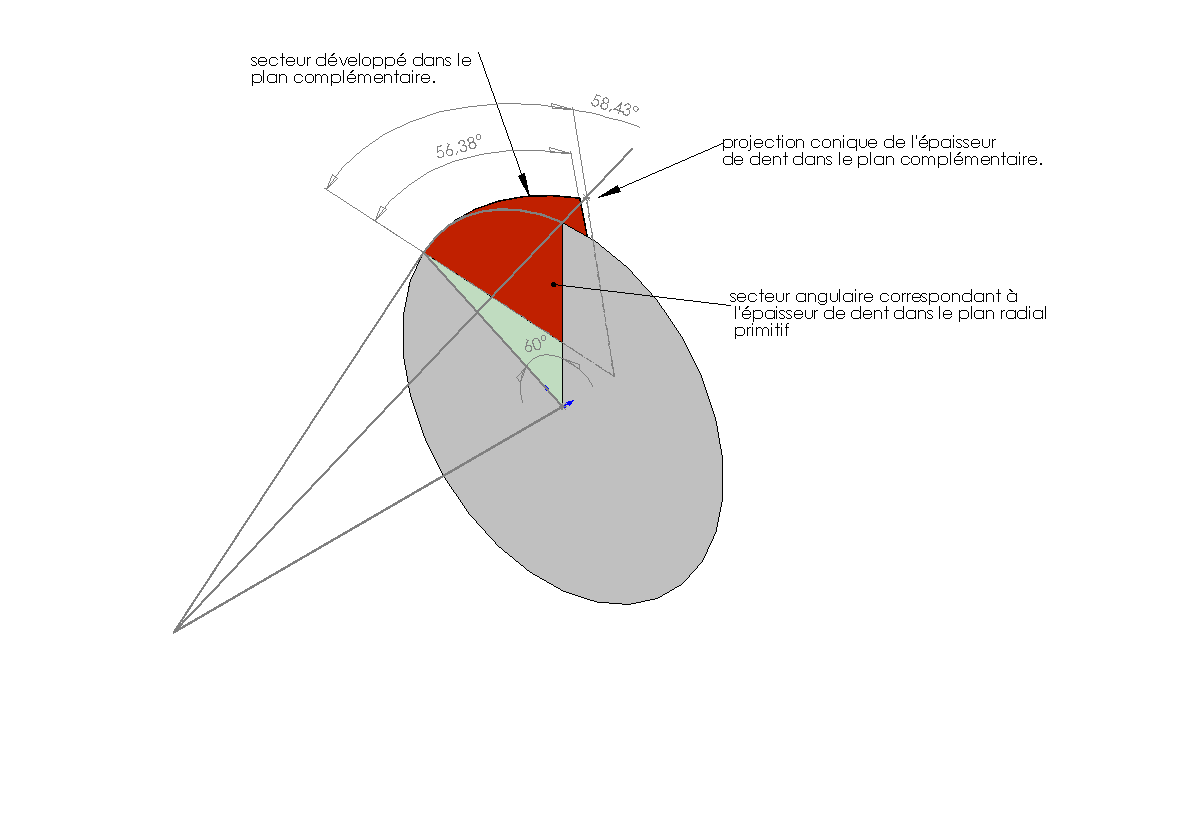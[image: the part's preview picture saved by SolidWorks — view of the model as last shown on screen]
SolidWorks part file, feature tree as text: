
SOLIDWORKS PART (.sldprt)
format: sldprt  version: not decoded by parser v0  size: 222,208 bytes
history: native  units: mm
features: sketch x7, plane x6, material x1, revolve x1, extrude x1 + 1 further entry (+10 scaffold rows collapsed)
feature tree (27):
  scaffold x10  (default folders/planes/origin — collapsed)
  material  "Matériau <non spécifié>"
  "Objet de détail6"  RD2=56.38deg RD3=60deg RD4=58.433296deg
  plane  "Plan de face"
  plane  "Plan de dessus"
  plane  "Plan de droite"
  sketch  "Esquisse1"  dims[c1.D1=~75.684225mm c2.D1=70.0deg c2.D2=200.0mm]
  revolve  "Révolution1"  Angle=300deg
  plane  "Plan1"
  plane  "Plan2"
  sketch  "Esquisse2"  dims[c1.D1=~212.835554mm c2.D1=56.38deg]
  extrude  "Extrusion1"  Depth=1mm
  sketch  "Esquisse3"
  sketch  "Esquisse4"
  sketch  "Esquisse3D1"
  sketch  "Esquisse5"  dims[c1.D1=~215.913418mm c2.D1=~58.433296deg]
  plane  "Plan3"
  sketch  "Esquisse6"  dims[c1.D1=~207.63167mm c2.D1=~56.048641deg]
decode coverage: 6 of 9 modeling features carry decoded parameters; 1 rows unclassified (native names shown)
note: ~ marks probable driven/reference dimensions
note: suppression state not decoded; provenance and decode notes live in map.json
